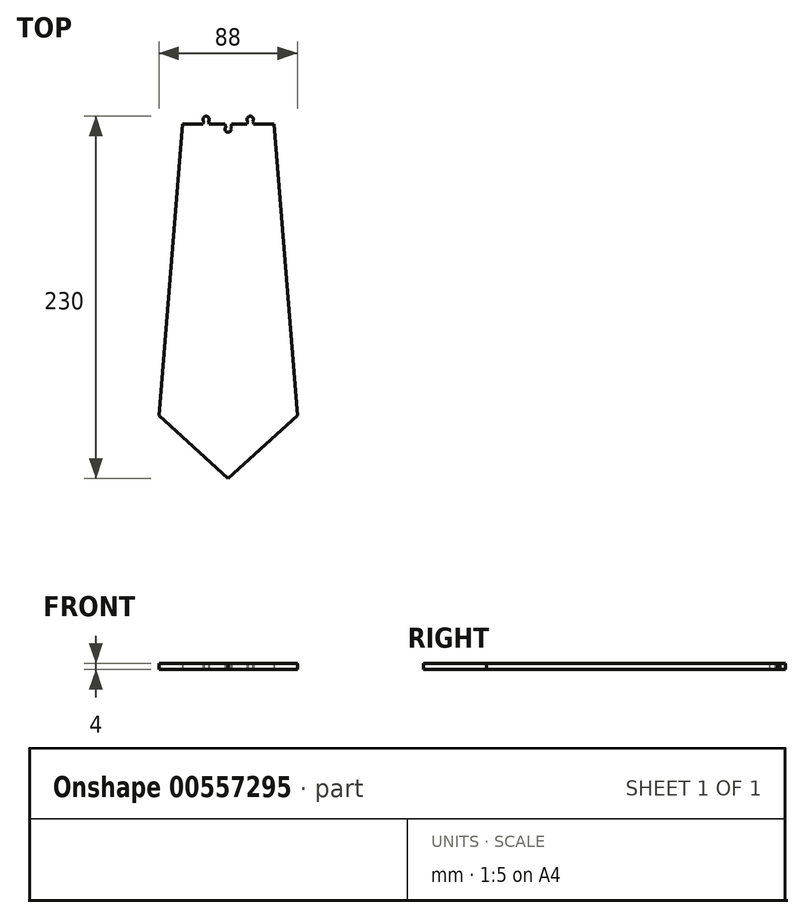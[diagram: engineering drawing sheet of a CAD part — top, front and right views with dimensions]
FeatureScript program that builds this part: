
annotation { "Feature Type Name" : "Feature", "Feature Type Description" : "" }
export const myFeature = defineFeature(function(context is Context, id is Id, definition is map)
    precondition{}
    {
        {
            var Q0;
            Q0=qCreatedBy(makeId("Top.planeOp"),FACE);
            var sketch = newSketch(context, id + "F0", { "sketchPlane" : qUnion([Q0])});
            skLineSegment(sketch, "E0", {"start": v(-1.09, 100.04) * mm, "end": v(-1.09, 94.88) * mm});
            skLineSegment(sketch, "E1", {"start": v(0.91, 100.04) * mm, "end": v(27.91, 100.04) * mm});
            skLineSegment(sketch, "E2", {"start": v(27.91, 100.04) * mm, "end": v(14.91, 100.04) * mm});
            skPoint(sketch, "E3", {"position": v(-15.09, 100.04) * mm});
            skPoint(sketch, "E4", {"position": v(-1.09, 100.04) * mm});
            skPoint(sketch, "E5", {"position": v(12.91, 100.04) * mm});
            skLineSegment(sketch, "E6", {"start": v(-17.09, 100.04) * mm, "end": v(-17.09, 101.04) * mm});
            skLineSegment(sketch, "E7", {"start": v(-13.09, 100.04) * mm, "end": v(-13.09, 101.04) * mm});
            skLineSegment(sketch, "E8", {"start": v(-3.09, 100.04) * mm, "end": v(-3.09, 99.04) * mm});
            skLineSegment(sketch, "E9", {"start": v(0.91, 100.04) * mm, "end": v(0.91, 98.88) * mm});
            skLineSegment(sketch, "E10", {"start": v(14.91, 100.04) * mm, "end": v(14.91, 101.04) * mm});
            skLineSegment(sketch, "E11", {"start": v(10.91, 100.04) * mm, "end": v(10.91, 101.04) * mm});
            skPoint(sketch, "E12", {"position": v(-1.09, 94.88) * mm});
            skArc(sketch, "E13", {"start": v(-2.42, 98.37) * mm, "mid": v(-1.14, 94.88) * mm, "end": v(0.33, 98.3) * mm});
            skLineSegment(sketch, "E14", {"start": v(-3.09, 99.04) * mm, "end": v(-2.42, 98.37) * mm});
            skPoint(sketch, "E15", {"position": v(12.91, 104.88) * mm});
            skArc(sketch, "E16", {"start": v(14.33, 101.63) * mm, "mid": v(12.91, 105.04) * mm, "end": v(11.5, 101.63) * mm});
            skLineSegment(sketch, "E17", {"start": v(10.91, 101.04) * mm, "end": v(11.5, 101.63) * mm});
            skArc(sketch, "E18", {"start": v(-13.67, 101.63) * mm, "mid": v(-15.09, 105.04) * mm, "end": v(-16.5, 101.63) * mm});
            skLineSegment(sketch, "E19", {"start": v(-13.09, 101.04) * mm, "end": v(-13.67, 101.63) * mm});
            skLineSegment(sketch, "E20", {"start": v(-17.09, 101.04) * mm, "end": v(-16.5, 101.63) * mm});
            skLineSegment(sketch, "E21.trimOffspring", {"start": v(-3.09, 100.04) * mm, "end": v(-13.09, 100.04) * mm});
            skLineSegment(sketch, "E22.trimOffspring", {"start": v(0.33, 98.3) * mm, "end": v(0.91, 98.88) * mm});
            skLineSegment(sketch, "E23.trimOffspring", {"start": v(14.33, 101.63) * mm, "end": v(14.91, 101.04) * mm});
            skLineSegment(sketch, "E24.trimOffspring", {"start": v(10.91, 100.04) * mm, "end": v(0.91, 100.04) * mm});
            skLineSegment(sketch, "E25.trimOffspring", {"start": v(-17.09, 100.04) * mm, "end": v(-30.09, 100.04) * mm});
            skPoint(sketch, "E26", {"position": v(-1.09, -84.96) * mm});
            skLineSegment(sketch, "E27", {"start": v(42.91, -84.96) * mm, "end": v(-1.09, -124.96) * mm});
            skLineSegment(sketch, "E28", {"start": v(-1.09, -124.96) * mm, "end": v(-45.09, -84.96) * mm});
            skLineSegment(sketch, "E29", {"start": v(-45.09, -84.96) * mm, "end": v(-30.09, 100.04) * mm});
            skLineSegment(sketch, "E30", {"start": v(27.91, 100.04) * mm, "end": v(42.91, -84.96) * mm});
            skSolve(sketch);
        }
        {
            var Q0;
            Q0 = qSketchRegion(id + "F0", true);
            extrude(context, id + "F1", {"entities" : qUnion([Q0]), "depth" : 4 * mm, "offsetDistance" : 25 * mm});
        }
    });
